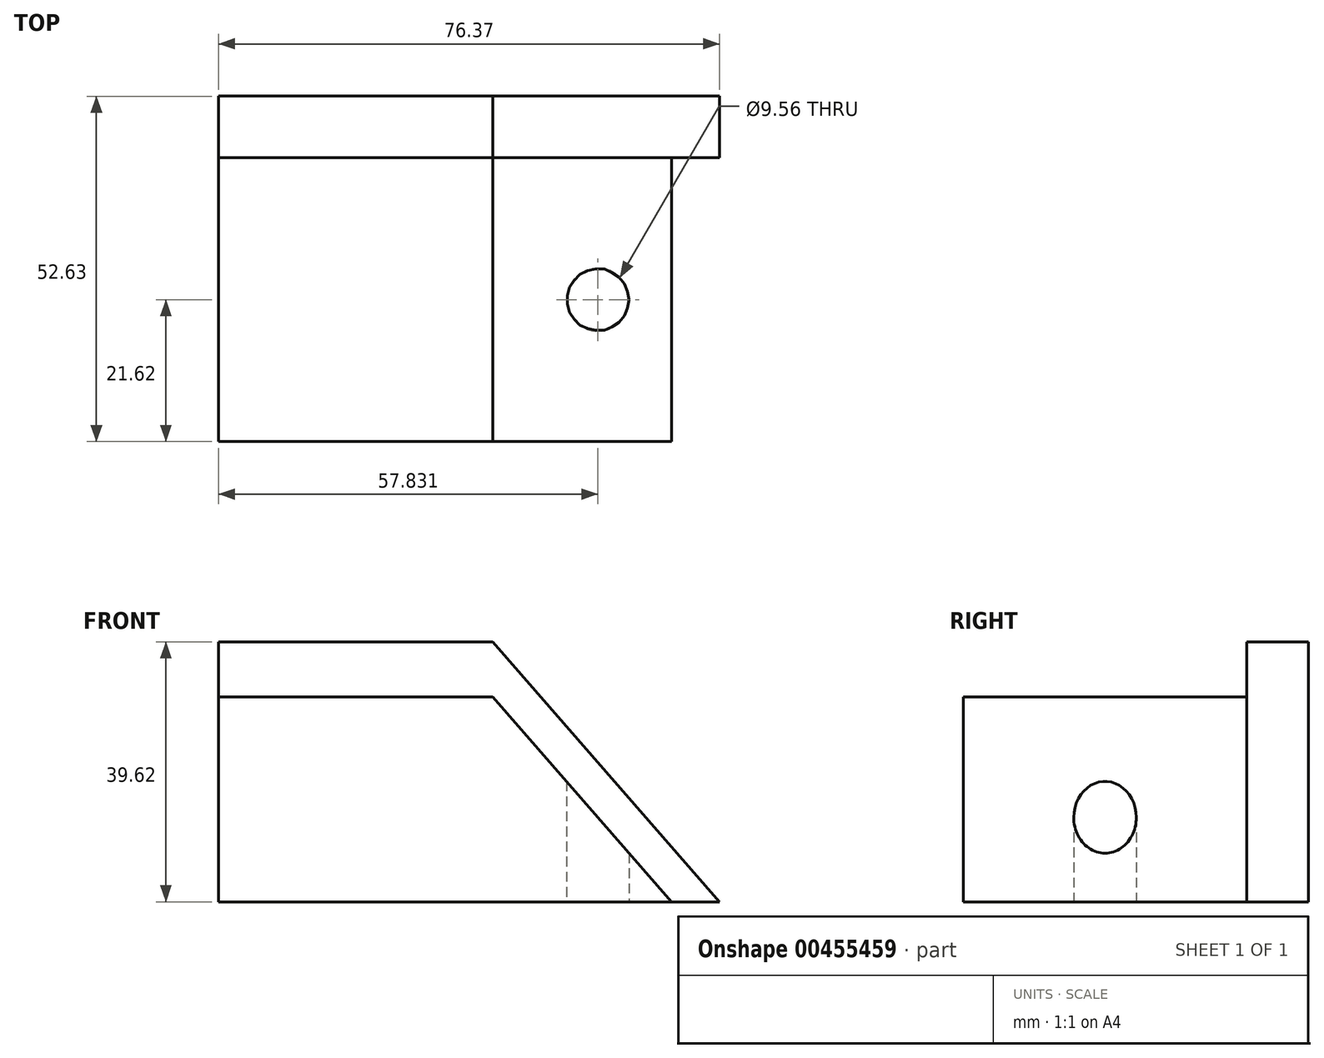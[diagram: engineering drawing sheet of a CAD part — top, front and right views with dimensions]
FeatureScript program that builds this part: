
annotation { "Feature Type Name" : "Feature", "Feature Type Description" : "" }
export const myFeature = defineFeature(function(context is Context, id is Id, definition is map)
    precondition{}
    {
        {
            var Q0;
            Q0=qCreatedBy(makeId("Top.planeOp"),FACE);
            var sketch = newSketch(context, id + "F0", { "sketchPlane" : qUnion([Q0])});
            skLineSegment(sketch, "E0.bottom", {"start": v(-34.53, 21.62) * mm, "end": v(34.53, 21.62) * mm});
            skLineSegment(sketch, "E0.top", {"start": v(-34.53, -21.62) * mm, "end": v(34.53, -21.62) * mm});
            skLineSegment(sketch, "E0.left", {"start": v(-34.53, 21.62) * mm, "end": v(-34.53, -21.62) * mm});
            skLineSegment(sketch, "E0.right", {"start": v(34.53, 21.62) * mm, "end": v(34.53, -21.62) * mm});
            skPoint(sketch, "E0.middle", {"position": v(0, 0) * mm});
            skCircle(sketch, "E1", {"center": v(23.3, 0) * mm, "radius": 4.78 * mm});
            skSolve(sketch);
        }
        {
            var Q0;
            Q0=makeQuery(id+"F0.imprint","IMPRINT",FACE,{"disambiguationData":[TD([[makeQuery(id+"F0.imprint","IMPRINT",EDGE,{"derivedFrom":sQuery(id+"F0.wireOp",EDGE,"E0.bottom")}),-1.0]])]});
            extrude(context, id + "F1", {"entities" : qUnion([Q0]), "depth" : 31.24 * mm});
        }
        {
            var Q0;
            Q0=makeQuery(id+"F1.opExtrude","SWEPT_FACE",FACE,{"disambiguationData":[OSD([sQuery(id+"F0.wireOp",EDGE,"E0.top")])]});
            var sketch = newSketch(context, id + "F2", { "sketchPlane" : qUnion([Q0])});
            skLineSegment(sketch, "E2", {"start": v(34.53, 0) * mm, "end": v(7.3, 31.24) * mm});
            skSolve(sketch);
        }
        {
            var Q0;
            {var subQ0=sQuery(id+"F2.wireOp",EDGE,"E2");Q0=makeQuery(id+"F2.imprint","IMPRINT",FACE,{"disambiguationData":[TD([[makeQuery(id+"F2.imprint","IMPRINT",EDGE,{"derivedFrom":subQ0}),-1.0]])]});}
            extrude(context, id + "F3", {"entities" : qUnion([Q0]), "operationType" : NewBodyOperationType.REMOVE, "oppositeDirection" : true, "depth" : 70.87 * mm});
        }
        {
            var Q0;
            Q0=makeQuery(id+"F1.opExtrude","SWEPT_FACE",FACE,{"disambiguationData":[OSD([sQuery(id+"F0.wireOp",EDGE,"E0.bottom")])]});
            extrude(context, id + "F4", {"entities" : qUnion([Q0]), "depth" : 9.4 * mm});
        }
        {
            var Q0;
            {var subQ0=sQuery(id+"F0.wireOp",EDGE,"E0.bottom");Q0=makeQuery(id+"F4.opExtrude","SWEPT_FACE",FACE,{"disambiguationData":[OSD([subQ0]),TDD([makeQuery(id+"F1.opExtrude","CAP_EDGE",EDGE,{"disambiguationData":[OSD([subQ0])],"isStart":false})])]});}
            var Q1;
            Q1=makeQuery(id+"F4.opExtrude","SWEPT_FACE",FACE,{"disambiguationData":[OSD([sQuery(id+"F0.wireOp",EDGE,"E0.bottom"),sQuery(id+"F2.wireOp",EDGE,"E2")])]});
            extrude(context, id + "F5", {"entities" : qUnion([Q0, Q1]), "operationType" : NewBodyOperationType.ADD, "depth" : 8.38 * mm});
        }
        {
            var Q0;
            {var subQ0=sQuery(id+"F2.wireOp",EDGE,"E2");var subQ1=sQuery(id+"F0.wireOp",EDGE,"E0.bottom");Q0=makeQuery(id+"F5.boolean.opBoolean","MERGE",FACE,{"derivedFrom":[makeQuery(id+"F4.opExtrude","CAP_FACE",FACE,{"disambiguationData":[OSD([subQ1])],"isStart":false}),makeQuery(id+"F5.opExtrude","SWEPT_FACE",FACE,{"disambiguationData":[OSD([subQ1]),TDD([makeQuery(id+"F4.opExtrude","CAP_EDGE",EDGE,{"disambiguationData":[OSD([subQ1]),TDD([makeQuery(id+"F1.opExtrude","CAP_EDGE",EDGE,{"disambiguationData":[OSD([subQ1])],"isStart":false})])],"isStart":false})])]}),makeQuery(id+"F5.opExtrude","SWEPT_FACE",FACE,{"disambiguationData":[OSD([subQ1,subQ0]),TDD([makeQuery(id+"F4.opExtrude","CAP_EDGE",EDGE,{"disambiguationData":[OSD([subQ1,subQ0])],"isStart":false})])]})]});}
            var sketch = newSketch(context, id + "F6", { "sketchPlane" : qUnion([Q0])});
            skLineSegment(sketch, "E3", {"start": v(-34.53, 8.38) * mm, "end": v(-41.84, 0) * mm});
            skLineSegment(sketch, "E4", {"start": v(-34.53, 0) * mm, "end": v(-41.84, 0) * mm});
            skLineSegment(sketch, "E5", {"start": v(-34.53, 0) * mm, "end": v(-34.53, 6.72) * mm});
            skLineSegment(sketch, "E6", {"start": v(-34.53, 6.72) * mm, "end": v(-34.53, 8.38) * mm});
            skSolve(sketch);
        }
        {
            var Q0;
            Q0=makeQuery(id+"F6.imprint","IMPRINT",FACE,{"disambiguationData":[TD([[makeQuery(id+"F6.imprint","IMPRINT",EDGE,{"derivedFrom":sQuery(id+"F6.wireOp",EDGE,"E3")}),1.0]])]});
            extrude(context, id + "F7", {"entities" : qUnion([Q0]), "operationType" : NewBodyOperationType.ADD, "oppositeDirection" : true, "depth" : 9.4 * mm});
        }
    });
